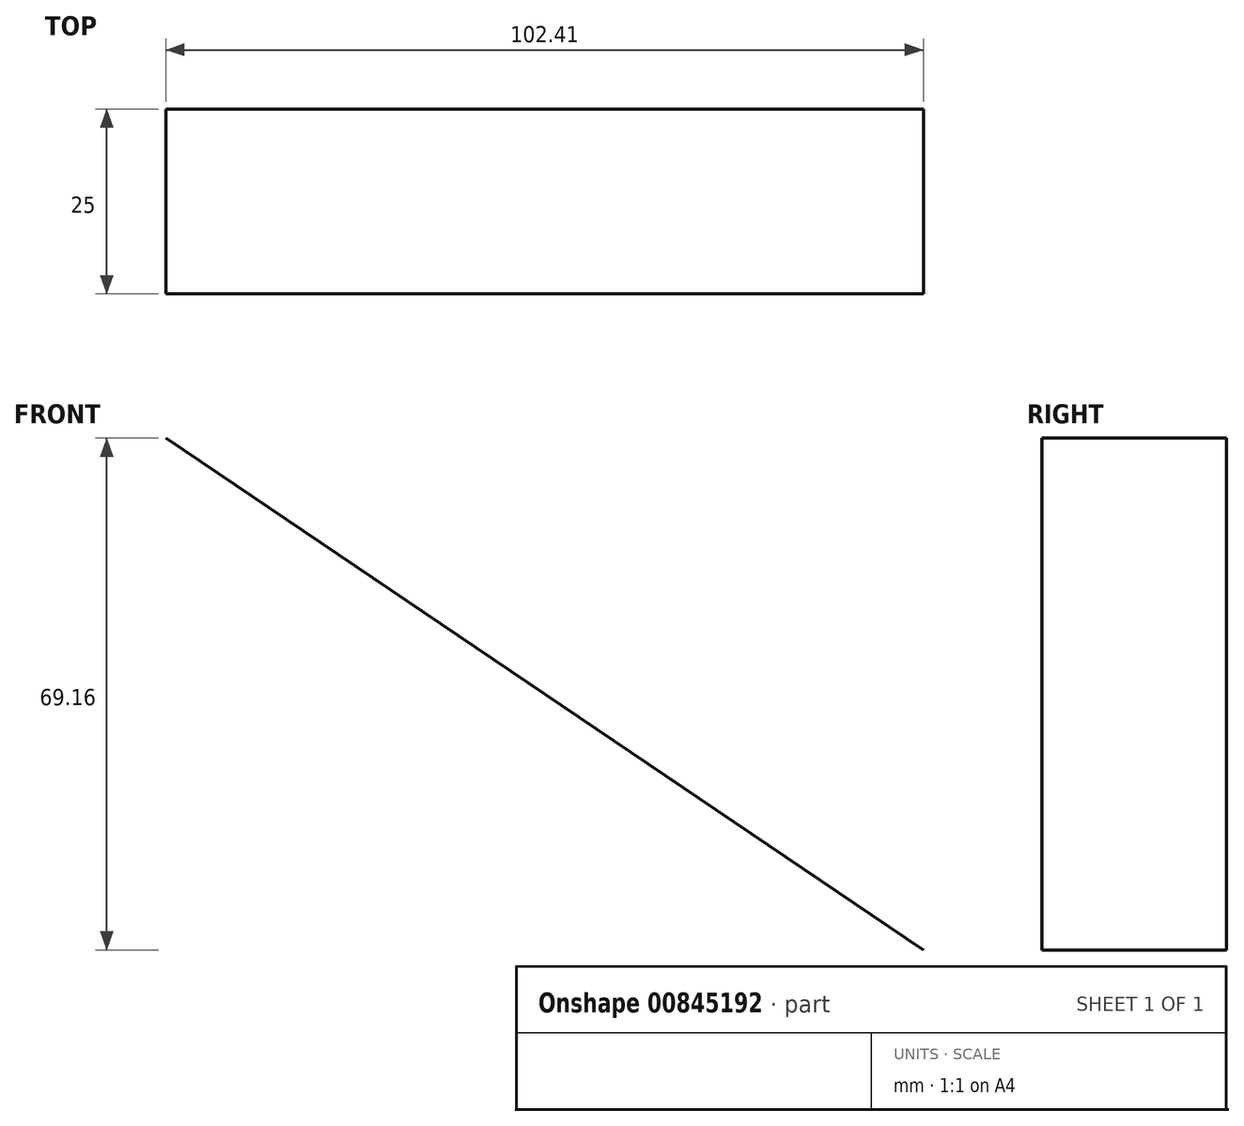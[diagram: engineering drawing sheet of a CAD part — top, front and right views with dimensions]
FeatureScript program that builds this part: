
annotation { "Feature Type Name" : "Feature", "Feature Type Description" : "" }
export const myFeature = defineFeature(function(context is Context, id is Id, definition is map)
    precondition{}
    {
        {
            var Q0;
            Q0=qCreatedBy(makeId("Front.planeOp"),FACE);
            var sketch = newSketch(context, id + "F0", { "sketchPlane" : qUnion([Q0])});
            skLineSegment(sketch, "E0", {"start": v(-55.09, 45.62) * mm, "end": v(47.32, -23.54) * mm});
            skSolve(sketch);
        }
        {
            var Q0;
            Q0=sQuery(id+"F0.wireOp",EDGE,"E0");
            extrude(context, id + "F1", {"bodyType" : ToolBodyType.SURFACE, "surfaceEntities" : qUnion([Q0]), "depth" : 25 * mm, "offsetDistance" : 25 * mm});
        }
    });
